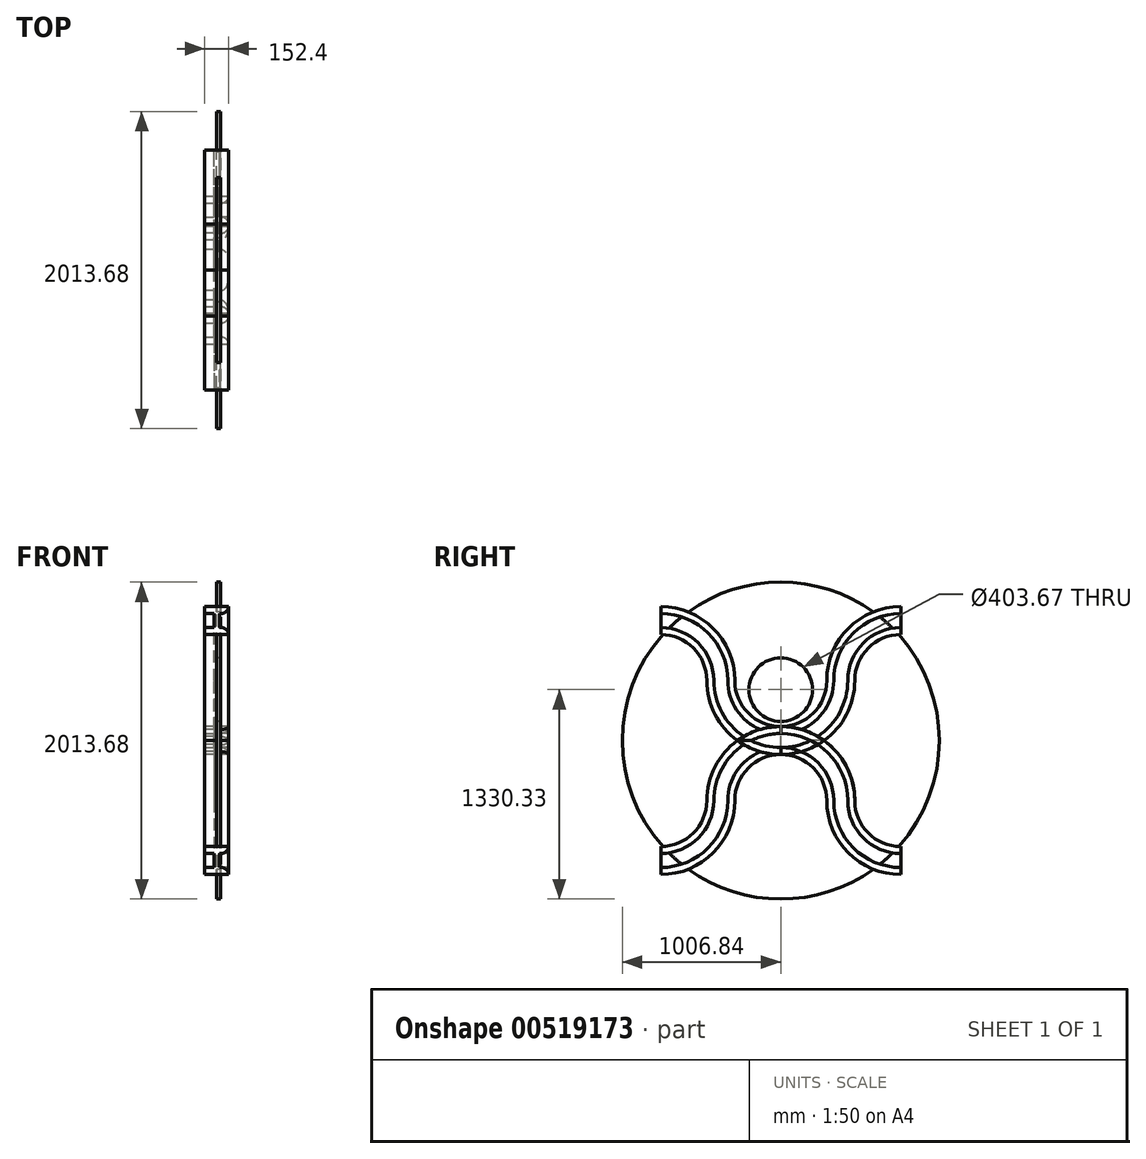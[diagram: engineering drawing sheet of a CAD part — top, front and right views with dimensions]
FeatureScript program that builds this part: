
annotation { "Feature Type Name" : "Feature", "Feature Type Description" : "" }
export const myFeature = defineFeature(function(context is Context, id is Id, definition is map)
    precondition{}
    {
        {
            var Q0;
            Q0=qCreatedBy(makeId("Front.planeOp"),FACE);
            var sketch = newSketch(context, id + "F0", { "sketchPlane" : qUnion([Q0])});
            skLineSegment(sketch, "E0", {"start": v(0, 88.9) * mm, "end": v(76.2, 88.9) * mm});
            skLineSegment(sketch, "E1", {"start": v(76.2, 88.9) * mm, "end": v(76.2, 44.45) * mm});
            skLineSegment(sketch, "E2", {"start": v(76.2, 44.45) * mm, "end": v(17.37, 44.45) * mm});
            skLineSegment(sketch, "E3", {"start": v(0, 88.9) * mm, "end": v(0, -88.9) * mm, "construction": true});
            skLineSegment(sketch, "E4", {"start": v(-17.37, 0) * mm, "end": v(17.37, 0) * mm, "construction": true});
            skLineSegment(sketch, "E5", {"start": v(17.37, 0) * mm, "end": v(17.37, 44.45) * mm});
            skLineSegment(sketch, "E6.MirrorCS", {"start": v(0, 88.9) * mm, "end": v(-76.2, 88.9) * mm});
            skLineSegment(sketch, "E7.MirrorCS", {"start": v(-76.2, 88.9) * mm, "end": v(-76.2, 44.45) * mm});
            skLineSegment(sketch, "E8.MirrorCS", {"start": v(-17.37, 0) * mm, "end": v(-17.37, 44.45) * mm});
            skLineSegment(sketch, "E9.MirrorCS", {"start": v(-76.2, 44.45) * mm, "end": v(-17.37, 44.45) * mm});
            skLineSegment(sketch, "E10.MirrorCS", {"start": v(0, -88.9) * mm, "end": v(-76.2, -88.9) * mm});
            skLineSegment(sketch, "E11.MirrorCS", {"start": v(-76.2, -88.9) * mm, "end": v(-76.2, -44.45) * mm});
            skLineSegment(sketch, "E12.MirrorCS", {"start": v(-76.2, -44.45) * mm, "end": v(-17.37, -44.45) * mm});
            skLineSegment(sketch, "E13.MirrorCS", {"start": v(-17.37, 0) * mm, "end": v(-17.37, -44.45) * mm});
            skLineSegment(sketch, "E14.MirrorCS", {"start": v(76.2, -44.45) * mm, "end": v(17.37, -44.45) * mm});
            skLineSegment(sketch, "E15.MirrorCS", {"start": v(0, -88.9) * mm, "end": v(76.2, -88.9) * mm});
            skLineSegment(sketch, "E16.MirrorCS", {"start": v(17.37, 0) * mm, "end": v(17.37, -44.45) * mm});
            skLineSegment(sketch, "E17.MirrorCS", {"start": v(76.2, -88.9) * mm, "end": v(76.2, -44.45) * mm});
            skSolve(sketch);
        }
        {
            var Q0;
            Q0=qCreatedBy(makeId("Right.planeOp"),FACE);
            var sketch = newSketch(context, id + "F1", { "sketchPlane" : qUnion([Q0])});
            skArc(sketch, "E18", {"start": v(0, 0) * mm, "mid": v(269.4, -111.6) * mm, "end": v(381, -381) * mm});
            skArc(sketch, "E19", {"start": v(381, -381) * mm, "mid": v(492.6, -650.4) * mm, "end": v(762, -762) * mm});
            skSolve(sketch);
        }
        {
            var Q0;
            Q0=makeQuery(id+"F0.imprint","IMPRINT",FACE,{"disambiguationData":[TD([[makeQuery(id+"F0.imprint","IMPRINT",EDGE,{"derivedFrom":sQuery(id+"F0.wireOp",EDGE,"E0")}),-1.0]])]});
            var Q1;
            Q1=sQuery(id+"F1.wireOp",EDGE,"E18");
            var Q2;
            Q2=sQuery(id+"F1.wireOp",EDGE,"E19");
            sweep(context, id + "F2", {"profiles" : qUnion([Q0]), "path" : qUnion([Q1, Q2])});
        }
        {
            var Q0;
            Q0=makeQuery(id+"F2.opSweep","SWEPT_EDGE",EDGE,{"disambiguationData":[OSD([sQuery(id+"F0.wireOp",EDGE,"E1"),sQuery(id+"F0.wireOp",EDGE,"E2"),sQuery(id+"F1.wireOp",EDGE,"E18")])]});
            var Q1;
            Q1=makeQuery(id+"F2.opSweep","SWEPT_EDGE",EDGE,{"disambiguationData":[OSD([sQuery(id+"F0.wireOp",EDGE,"E1"),sQuery(id+"F0.wireOp",EDGE,"E2"),sQuery(id+"F1.wireOp",EDGE,"E19")])]});
            fillet(context, id + "F3", {"entities" : qUnion([Q0, Q1]), "radius" : 50.8 * mm, "tangentPropagation" : true, "allowEdgeOverflow" : false});
        }
        {
            var Q0;
            Q0=makeQuery(id+"F2.opSweep","SWEPT_EDGE",EDGE,{"disambiguationData":[OSD([sQuery(id+"F0.wireOp",EDGE,"E14.MirrorCS"),sQuery(id+"F0.wireOp",EDGE,"E17.MirrorCS"),sQuery(id+"F1.wireOp",EDGE,"E18")])]});
            var Q1;
            Q1=makeQuery(id+"F2.opSweep","SWEPT_EDGE",EDGE,{"disambiguationData":[OSD([sQuery(id+"F0.wireOp",EDGE,"E14.MirrorCS"),sQuery(id+"F0.wireOp",EDGE,"E17.MirrorCS"),sQuery(id+"F1.wireOp",EDGE,"E19")])]});
            fillet(context, id + "F4", {"entities" : qUnion([Q0, Q1]), "radius" : 50.8 * mm, "tangentPropagation" : true, "allowEdgeOverflow" : false});
        }
        {
            var Q0;
            Q0=makeQuery(id+"F2.opSweep","SWEPT_BODY",BODY,{"disambiguationData":[OSD([sQuery(id+"F0.wireOp",EDGE,"E0"),sQuery(id+"F0.wireOp",EDGE,"E1"),sQuery(id+"F0.wireOp",EDGE,"E2"),sQuery(id+"F0.wireOp",EDGE,"E5"),sQuery(id+"F0.wireOp",EDGE,"E6.MirrorCS"),sQuery(id+"F0.wireOp",EDGE,"E8.MirrorCS"),sQuery(id+"F0.wireOp",EDGE,"E9.MirrorCS"),sQuery(id+"F0.wireOp",EDGE,"E7.MirrorCS"),sQuery(id+"F0.wireOp",EDGE,"E10.MirrorCS"),sQuery(id+"F0.wireOp",EDGE,"E11.MirrorCS"),sQuery(id+"F0.wireOp",EDGE,"E12.MirrorCS"),sQuery(id+"F0.wireOp",EDGE,"E13.MirrorCS"),sQuery(id+"F0.wireOp",EDGE,"E14.MirrorCS"),sQuery(id+"F0.wireOp",EDGE,"E15.MirrorCS"),sQuery(id+"F0.wireOp",EDGE,"E16.MirrorCS"),sQuery(id+"F0.wireOp",EDGE,"E17.MirrorCS"),sQuery(id+"F1.wireOp",EDGE,"E19")])]});
            var Q1;
            Q1=qCreatedBy(makeId("Front.planeOp"),FACE);
            mirror(context, id + "F5", {"operationType" : NewBodyOperationType.ADD, "entities" : qUnion([Q0]), "mirrorPlane" : qUnion([Q1])});
        }
        {
            var Q0;
            Q0=makeQuery(id+"F2.opSweep","SWEPT_BODY",BODY,{"disambiguationData":[OSD([sQuery(id+"F0.wireOp",EDGE,"E0"),sQuery(id+"F0.wireOp",EDGE,"E1"),sQuery(id+"F0.wireOp",EDGE,"E2"),sQuery(id+"F0.wireOp",EDGE,"E5"),sQuery(id+"F0.wireOp",EDGE,"E6.MirrorCS"),sQuery(id+"F0.wireOp",EDGE,"E8.MirrorCS"),sQuery(id+"F0.wireOp",EDGE,"E9.MirrorCS"),sQuery(id+"F0.wireOp",EDGE,"E7.MirrorCS"),sQuery(id+"F0.wireOp",EDGE,"E10.MirrorCS"),sQuery(id+"F0.wireOp",EDGE,"E11.MirrorCS"),sQuery(id+"F0.wireOp",EDGE,"E12.MirrorCS"),sQuery(id+"F0.wireOp",EDGE,"E13.MirrorCS"),sQuery(id+"F0.wireOp",EDGE,"E14.MirrorCS"),sQuery(id+"F0.wireOp",EDGE,"E15.MirrorCS"),sQuery(id+"F0.wireOp",EDGE,"E16.MirrorCS"),sQuery(id+"F0.wireOp",EDGE,"E17.MirrorCS"),sQuery(id+"F1.wireOp",EDGE,"E19")])]});
            var Q1;
            Q1=qCreatedBy(makeId("Top.planeOp"),FACE);
            mirror(context, id + "F6", {"operationType" : NewBodyOperationType.ADD, "entities" : qUnion([Q0]), "mirrorPlane" : qUnion([Q1])});
        }
        {
            var Q0;
            Q0=qCreatedBy(makeId("Right.planeOp"),FACE);
            var sketch = newSketch(context, id + "F7", { "sketchPlane" : qUnion([Q0])});
            skCircle(sketch, "E20", {"center": v(0, 0) * mm, "radius": 1006.84 * mm});
            skCircle(sketch, "E21", {"center": v(0, 323.49) * mm, "radius": 201.84 * mm});
            skSolve(sketch);
        }
        {
            var Q0;
            Q0=makeQuery(id+"F7.imprint","IMPRINT",FACE,{"disambiguationData":[TD([[makeQuery(id+"F7.imprint","IMPRINT",EDGE,{"derivedFrom":sQuery(id+"F7.wireOp",EDGE,"E20")}),1.0]])]});
            extrude(context, id + "F8", {"entities" : qUnion([Q0]), "operationType" : NewBodyOperationType.ADD, "depth" : 25.4 * mm});
        }
        {
            var Q0;
            Q0=makeQuery(id+"F0.imprint","IMPRINT",FACE,{"disambiguationData":[TD([[makeQuery(id+"F0.imprint","IMPRINT",EDGE,{"derivedFrom":sQuery(id+"F0.wireOp",EDGE,"E0")}),-1.0]])]});
            var Q1;
            Q1=sQuery(id+"F1.wireOp",EDGE,"E18");
            var Q2;
            Q2=sQuery(id+"F1.wireOp",EDGE,"E19");
            sweep(context, id + "F9", {"profiles" : qUnion([Q0]), "path" : qUnion([Q1, Q2])});
        }
    });
